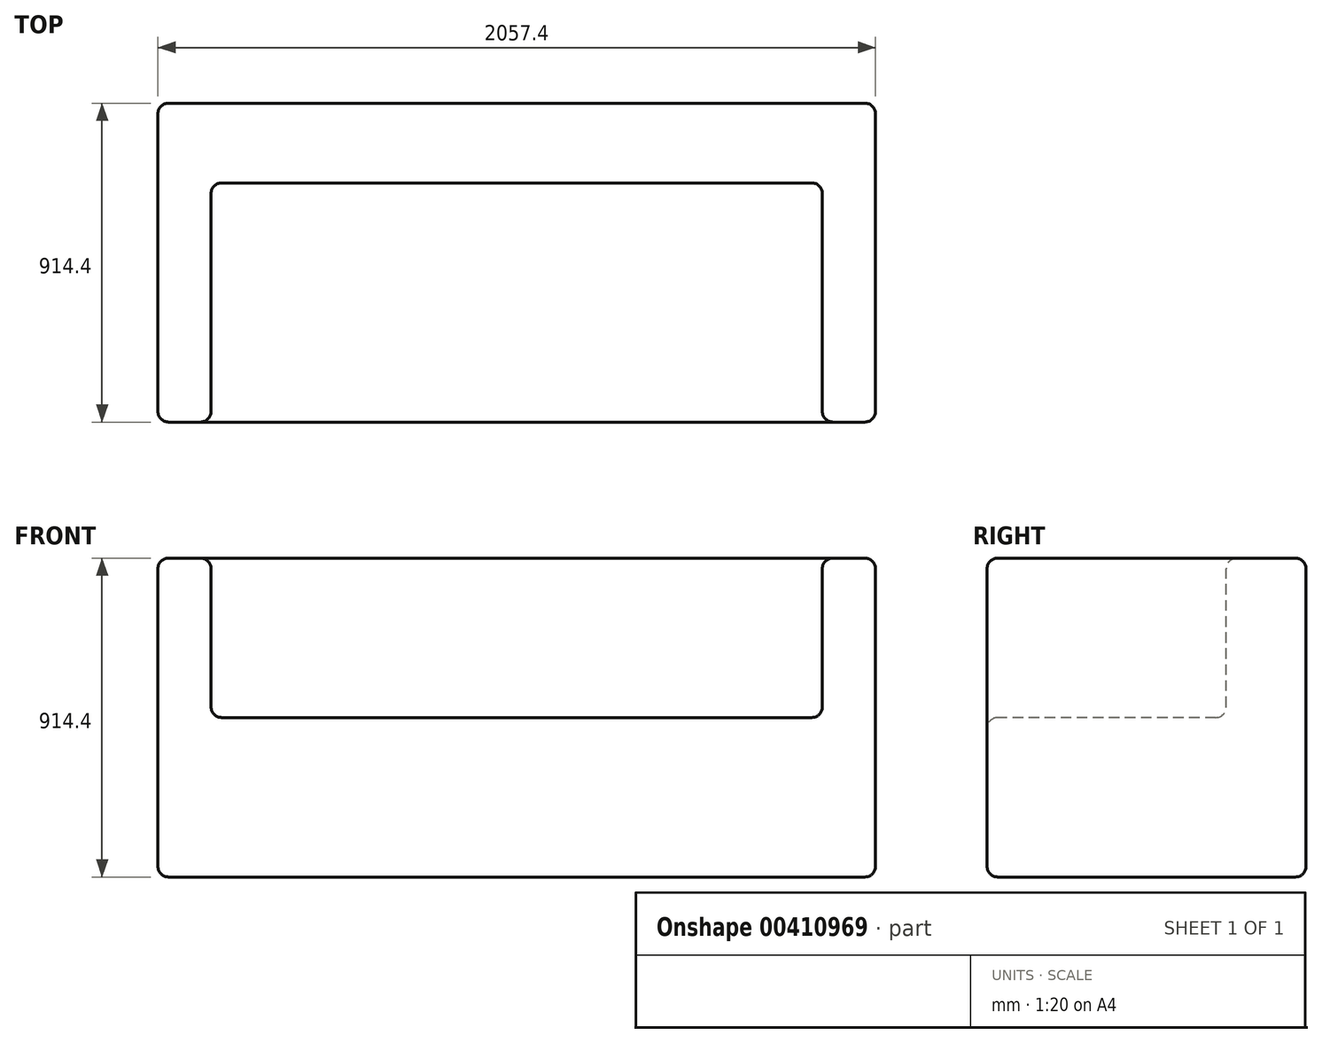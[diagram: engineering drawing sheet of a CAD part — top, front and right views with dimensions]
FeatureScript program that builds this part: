
annotation { "Feature Type Name" : "Feature", "Feature Type Description" : "" }
export const myFeature = defineFeature(function(context is Context, id is Id, definition is map)
    precondition{}
    {
        {
            var Q0;
            Q0=qCreatedBy(makeId("Top.planeOp"),FACE);
            var sketch = newSketch(context, id + "F0", { "sketchPlane" : qUnion([Q0])});
            skLineSegment(sketch, "E0.bottom", {"start": v(1028.7, -457.2) * mm, "end": v(-1028.7, -457.2) * mm});
            skLineSegment(sketch, "E0.top", {"start": v(1028.7, 457.2) * mm, "end": v(-1028.7, 457.2) * mm});
            skLineSegment(sketch, "E0.left", {"start": v(1028.7, -457.2) * mm, "end": v(1028.7, 457.2) * mm});
            skLineSegment(sketch, "E0.right", {"start": v(-1028.7, -457.2) * mm, "end": v(-1028.7, 457.2) * mm});
            skPoint(sketch, "E0.middle", {"position": v(0, 0) * mm});
            skSolve(sketch);
        }
        {
            var Q0;
            Q0=makeQuery(id+"F0.imprint","IMPRINT",FACE,{"disambiguationData":[TD([[makeQuery(id+"F0.imprint","IMPRINT",EDGE,{"derivedFrom":sQuery(id+"F0.wireOp",EDGE,"E0.bottom")}),-1.0]])]});
            extrude(context, id + "F1", {"entities" : qUnion([Q0]), "depth" : 914.4 * mm});
        }
        {
            var Q0;
            Q0=makeQuery(id+"F1.opExtrude","CAP_FACE",FACE,{"disambiguationData":[OSD([sQuery(id+"F0.wireOp",EDGE,"E0.bottom"),sQuery(id+"F0.wireOp",EDGE,"E0.top"),sQuery(id+"F0.wireOp",EDGE,"E0.left"),sQuery(id+"F0.wireOp",EDGE,"E0.right")])],"isStart":false});
            var sketch = newSketch(context, id + "F2", { "sketchPlane" : qUnion([Q0])});
            skLineSegment(sketch, "E1", {"start": v(-876.3, -457.2) * mm, "end": v(-876.3, 228.6) * mm});
            skLineSegment(sketch, "E2", {"start": v(-876.3, 228.6) * mm, "end": v(876.3, 228.6) * mm});
            skLineSegment(sketch, "E3", {"start": v(876.3, 228.6) * mm, "end": v(876.3, -457.2) * mm});
            skSolve(sketch);
        }
        {
            var Q0;
            {var subQ0=sQuery(id+"F2.wireOp",EDGE,"E1");Q0=makeQuery(id+"F2.imprint","IMPRINT",FACE,{"disambiguationData":[TD([[makeQuery(id+"F2.imprint","IMPRINT",EDGE,{"derivedFrom":subQ0}),-1.0]])]});}
            extrude(context, id + "F3", {"entities" : qUnion([Q0]), "operationType" : NewBodyOperationType.REMOVE, "oppositeDirection" : true, "depth" : 457.2 * mm});
        }
        {
            var Q0;
            Q0=makeQuery(id+"F3.boolean.opBoolean","COPY",FACE,{"derivedFrom":makeQuery(id+"F3.opExtrude","CAP_FACE",FACE,{"disambiguationData":[OSD([sQuery(id+"F0.wireOp",EDGE,"E0.bottom"),sQuery(id+"F2.wireOp",EDGE,"E1"),sQuery(id+"F2.wireOp",EDGE,"E2"),sQuery(id+"F2.wireOp",EDGE,"E3")])],"isStart":false})});
            var Q1;
            Q1=makeQuery(id+"F3.boolean.opBoolean","COPY",FACE,{"derivedFrom":makeQuery(id+"F3.opExtrude","SWEPT_FACE",FACE,{"disambiguationData":[OSD([sQuery(id+"F2.wireOp",EDGE,"E1")])]})});
            var Q2;
            Q2=makeQuery(id+"F3.boolean.opBoolean","COPY",FACE,{"derivedFrom":makeQuery(id+"F3.opExtrude","SWEPT_FACE",FACE,{"disambiguationData":[OSD([sQuery(id+"F2.wireOp",EDGE,"E2")])]})});
            var Q3;
            Q3=makeQuery(id+"F1.opExtrude","SWEPT_FACE",FACE,{"disambiguationData":[OSD([sQuery(id+"F0.wireOp",EDGE,"E0.bottom")])]});
            var Q4;
            Q4=makeQuery(id+"F1.opExtrude","CAP_FACE",FACE,{"disambiguationData":[OSD([sQuery(id+"F0.wireOp",EDGE,"E0.bottom"),sQuery(id+"F0.wireOp",EDGE,"E0.top"),sQuery(id+"F0.wireOp",EDGE,"E0.left"),sQuery(id+"F0.wireOp",EDGE,"E0.right")])],"isStart":false});
            var Q5;
            Q5=makeQuery(id+"F1.opExtrude","SWEPT_FACE",FACE,{"disambiguationData":[OSD([sQuery(id+"F0.wireOp",EDGE,"E0.left")])]});
            var Q6;
            Q6=makeQuery(id+"F1.opExtrude","SWEPT_FACE",FACE,{"disambiguationData":[OSD([sQuery(id+"F0.wireOp",EDGE,"E0.right")])]});
            var Q7;
            Q7=makeQuery(id+"F1.opExtrude","SWEPT_FACE",FACE,{"disambiguationData":[OSD([sQuery(id+"F0.wireOp",EDGE,"E0.top")])]});
            fillet(context, id + "F4", {"entities" : qUnion([Q0, Q1, Q2, Q3, Q4, Q5, Q6, Q7]), "radius" : 30.48 * mm, "tangentPropagation" : true, "allowEdgeOverflow" : false});
        }
    });
